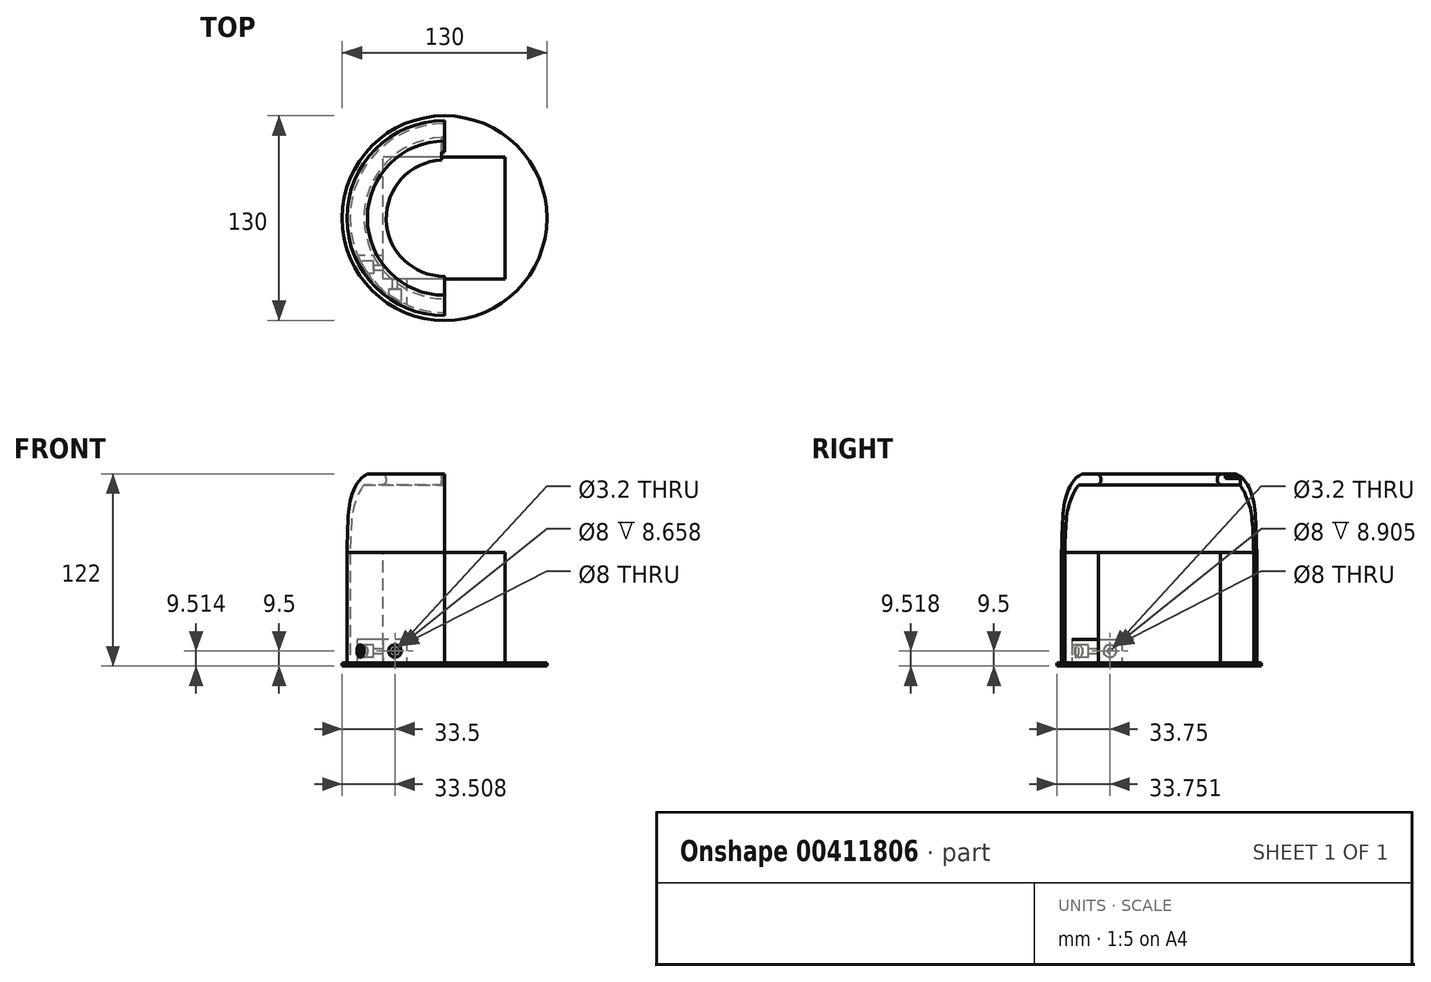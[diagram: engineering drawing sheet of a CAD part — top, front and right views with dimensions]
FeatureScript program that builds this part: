
annotation { "Feature Type Name" : "Feature", "Feature Type Description" : "" }
export const myFeature = defineFeature(function(context is Context, id is Id, definition is map)
    precondition{}
    {
        {
            var Q0;
            Q0=qCreatedBy(makeId("Front.planeOp"),FACE);
            var sketch = newSketch(context, id + "F0", { "sketchPlane" : qUnion([Q0])});
            skLineSegment(sketch, "E0", {"start": v(-40, 50) * mm, "end": v(-49, 50) * mm});
            skLineSegment(sketch, "E1", {"start": v(-62, 0) * mm, "end": v(-62, -70) * mm});
            skLineSegment(sketch, "E2", {"start": v(-37, 47) * mm, "end": v(-37, 46) * mm});
            skLineSegment(sketch, "E3", {"start": v(-40, 43) * mm, "end": v(-51.2, 43) * mm});
            skFitSpline(sketch, "E4", {"points": [v(-49, 50) * mm, v(-52.64, 47.47) * mm, v(-56.76, 41.98) * mm, v(-60.39, 29.9) * mm, v(-62, 0) * mm], "startDerivative": vector(-21.37, -10.6) * mm, "endDerivative": vector(-3.86, -109.3) * mm});
            skPoint(sketch, "E5.visualSharp", {"position": v(-37, 50) * mm});
            skArc(sketch, "E5.filletArc", {"start": v(-37, 47) * mm, "mid": v(-37.88, 49.12) * mm, "end": v(-40, 50) * mm});
            skPoint(sketch, "E6.visualSharp", {"position": v(-37, 43) * mm});
            skArc(sketch, "E6.filletArc", {"start": v(-40, 43) * mm, "mid": v(-37.88, 43.88) * mm, "end": v(-37, 46) * mm});
            skFitSpline(sketch, "E7", {"points": [v(-51.2, 43) * mm, v(-53.22, 40.09) * mm, v(-57.32, 30.2) * mm, v(-60, 0) * mm], "startDerivative": vector(-23.74, -33.12) * mm, "endDerivative": vector(-3.58, -89.87) * mm});
            skLineSegment(sketch, "E8", {"start": v(-62, -70) * mm, "end": v(0, -70) * mm});
            skLineSegment(sketch, "E9", {"start": v(0, -70) * mm, "end": v(0, -69.08) * mm});
            skLineSegment(sketch, "E10", {"start": v(-60, 0) * mm, "end": v(-60, -70) * mm});
            skSolve(sketch);
        }
        {
            var Q0;
            Q0=makeQuery(id+"F0.imprint","IMPRINT",FACE,{"disambiguationData":[TD([[makeQuery(id+"F0.imprint","IMPRINT",EDGE,{"derivedFrom":sQuery(id+"F0.wireOp",EDGE,"E0")}),1.0]])]});
            var Q1;
            Q1=sQuery(id+"F0.wireOp",EDGE,"E9");
            revolve(context, id + "F1", {"entities" : qUnion([Q0]), "axis" : qUnion([Q1]), "revolveType" : RevolveType.SYMMETRIC, "angle" : 180 * degree});
        }
        {
            var Q0;
            Q0=qCreatedBy(makeId("Front.planeOp"),FACE);
            var sketch = newSketch(context, id + "F2", { "sketchPlane" : qUnion([Q0])});
            skCircle(sketch, "E11", {"center": v(0, 47) * mm, "radius": 2 * mm});
            skLineSegment(sketch, "E12", {"start": v(-2, 47.07) * mm, "end": v(-2, 42.07) * mm});
            skLineSegment(sketch, "E13", {"start": v(-2, 42.07) * mm, "end": v(0, 42.07) * mm});
            skLineSegment(sketch, "E14", {"start": v(0, 42.07) * mm, "end": v(0, 45) * mm});
            skLineSegment(sketch, "E15", {"start": v(-2, 47.07) * mm, "end": v(-2, 50.36) * mm});
            skLineSegment(sketch, "E16", {"start": v(0, 50.36) * mm, "end": v(0, 49) * mm});
            skLineSegment(sketch, "E17", {"start": v(-2, 50.36) * mm, "end": v(0, 50.36) * mm});
            skSolve(sketch);
        }
        {
            var Q0;
            {var subQ1=sQuery(id+"F2.wireOp",EDGE,"E11");var subQ4=makeQuery(id+"F2.imprint","INTERSECT",VERTEX,{"derivedFrom":[subQ1,sQuery(id+"F2.wireOp",EDGE,"E14")]});Q0=makeQuery(id+"F2.imprint","IMPRINT",FACE,{"disambiguationData":[TD([[makeQuery(id+"F2.imprint","IMPRINT",EDGE,{"disambiguationData":[TD([[subQ4,1.0]])],"derivedFrom":subQ1}),1.0]])]});}
            extrude(context, id + "F3", {"entities" : qUnion([Q0]), "operationType" : NewBodyOperationType.REMOVE, "oppositeDirection" : true, "depth" : 49 * mm});
        }
        {
            var Q0;
            {var subQ0=sQuery(id+"F2.wireOp",EDGE,"E15");Q0=makeQuery(id+"F2.imprint","IMPRINT",FACE,{"disambiguationData":[TD([[makeQuery(id+"F2.imprint","IMPRINT",EDGE,{"derivedFrom":subQ0}),-1.0]])]});}
            extrude(context, id + "F4", {"entities" : qUnion([Q0]), "operationType" : NewBodyOperationType.REMOVE, "oppositeDirection" : true, "depth" : 42 * mm});
        }
        {
            var Q0;
            {var subQ4=sQuery(id+"F2.wireOp",EDGE,"E13");Q0=makeQuery(id+"F2.imprint","IMPRINT",FACE,{"disambiguationData":[TD([[makeQuery(id+"F2.imprint","IMPRINT",EDGE,{"derivedFrom":subQ4}),1.0]])]});}
            extrude(context, id + "F5", {"entities" : qUnion([Q0]), "operationType" : NewBodyOperationType.REMOVE, "oppositeDirection" : true, "depth" : 51.5 * mm});
        }
        {
            var Q0;
            Q0=qCreatedBy(makeId("Right.planeOp"),FACE);
            var sketch = newSketch(context, id + "F6", { "sketchPlane" : qUnion([Q0])});
            skLineSegment(sketch, "E18.bottom", {"start": v(49, 47) * mm, "end": v(51.5, 47) * mm});
            skLineSegment(sketch, "E18.top", {"start": v(49, 44) * mm, "end": v(51.5, 44) * mm});
            skLineSegment(sketch, "E18.left", {"start": v(49, 47) * mm, "end": v(49, 44) * mm});
            skLineSegment(sketch, "E18.right", {"start": v(51.5, 47) * mm, "end": v(51.5, 44) * mm});
            skSolve(sketch);
        }
        {
            var Q0;
            Q0=makeQuery(id+"F6.imprint","IMPRINT",FACE,{"disambiguationData":[TD([[makeQuery(id+"F6.imprint","IMPRINT",EDGE,{"derivedFrom":sQuery(id+"F6.wireOp",EDGE,"E18.bottom")}),-1.0]])]});
            extrude(context, id + "F7", {"entities" : qUnion([Q0]), "operationType" : NewBodyOperationType.REMOVE, "oppositeDirection" : true, "depth" : 2 * mm});
        }
        {
            var Q0;
            Q0=qCreatedBy(makeId("Top.planeOp"),FACE);
            var sketch = newSketch(context, id + "F8", { "sketchPlane" : qUnion([Q0])});
            skLineSegment(sketch, "E19.bottom", {"start": v(38.5, -38.75) * mm, "end": v(-39, -38.75) * mm});
            skLineSegment(sketch, "E19.top", {"start": v(38.5, 38.75) * mm, "end": v(-39, 38.75) * mm});
            skLineSegment(sketch, "E19.left", {"start": v(38.5, -38.75) * mm, "end": v(38.5, 38.75) * mm});
            skLineSegment(sketch, "E19.right", {"start": v(-39, -38.75) * mm, "end": v(-39, 38.75) * mm});
            skSolve(sketch);
        }
        {
            var Q0;
            Q0=makeQuery(id+"F8.imprint","IMPRINT",FACE,{"disambiguationData":[TD([[makeQuery(id+"F8.imprint","IMPRINT",EDGE,{"derivedFrom":sQuery(id+"F8.wireOp",EDGE,"E19.bottom")}),-1.0]])]});
            extrude(context, id + "F9", {"entities" : qUnion([Q0]), "operationType" : NewBodyOperationType.ADD, "oppositeDirection" : true, "depth" : 70 * mm});
        }
        {
            var Q0;
            Q0=makeQuery(id+"F9.opExtrude","CAP_FACE",FACE,{"disambiguationData":[OSD([sQuery(id+"F8.wireOp",EDGE,"E19.bottom"),sQuery(id+"F8.wireOp",EDGE,"E19.top"),sQuery(id+"F8.wireOp",EDGE,"E19.left"),sQuery(id+"F8.wireOp",EDGE,"E19.right")])],"isStart":false});
            var sketch = newSketch(context, id + "F10", { "sketchPlane" : qUnion([Q0])});
            skLineSegment(sketch, "E20", {"start": v(-39, 38.75) * mm, "end": v(-39, 23.75) * mm});
            skLineSegment(sketch, "E21", {"start": v(-39, 23.75) * mm, "end": v(-55.5, 23.75) * mm});
            skLineSegment(sketch, "E22", {"start": v(-39, 38.75) * mm, "end": v(-24, 38.75) * mm});
            skLineSegment(sketch, "E23", {"start": v(-24, 38.75) * mm, "end": v(-24, 55.25) * mm});
            skArc(sketch, "E24", {"start": v(-24, 55.25) * mm, "mid": v(-42.86, 42.6) * mm, "end": v(-55.5, 23.75) * mm});
            skSolve(sketch);
        }
        {
            var Q0;
            Q0=makeQuery(id+"F10.imprint","IMPRINT",FACE,{"disambiguationData":[TD([[makeQuery(id+"F10.imprint","IMPRINT",EDGE,{"derivedFrom":sQuery(id+"F10.wireOp",EDGE,"E20")}),-1.0]])]});
            extrude(context, id + "F11", {"entities" : qUnion([Q0]), "oppositeDirection" : true, "depth" : 15 * mm});
        }
        {
            var Q0;
            Q0=makeQuery(id+"F11.opExtrude","SWEPT_FACE",FACE,{"disambiguationData":[OSD([sQuery(id+"F10.wireOp",EDGE,"E20")])]});
            var sketch = newSketch(context, id + "F12", { "sketchPlane" : qUnion([Q0])});
            skCircle(sketch, "E25", {"center": v(-31.25, -62.5) * mm, "radius": 1.6 * mm});
            skSolve(sketch);
        }
        {
            var Q0;
            Q0=makeQuery(id+"F12.imprint","IMPRINT",FACE,{"disambiguationData":[TD([[makeQuery(id+"F12.imprint","IMPRINT",EDGE,{"derivedFrom":sQuery(id+"F12.wireOp",EDGE,"E25")}),1.0]])]});
            extrude(context, id + "F13", {"entities" : qUnion([Q0]), "operationType" : NewBodyOperationType.REMOVE, "oppositeDirection" : true, "depth" : 15 * mm});
        }
        {
            var Q0;
            Q0=qCreatedBy(makeId("Right.planeOp"),FACE);
            cPlane(context, id + "F14", {"entities" : qUnion([Q0]), "cplaneType" : CPlaneType.OFFSET, "offset" : 60 * mm, "oppositeDirection" : true, "width" : 150 * mm, "height" : 150 * mm});
        }
        {
            var Q0;
            Q0=qCreatedBy(id+"F14.planeOp",FACE);
            var sketch = newSketch(context, id + "F15", { "sketchPlane" : qUnion([Q0])});
            skCircle(sketch, "E26", {"center": v(-31.25, -62.48) * mm, "radius": 4 * mm});
            skSolve(sketch);
        }
        {
            var Q0;
            Q0 = qSketchRegion(id + "F15", true);
            extrude(context, id + "F16", {"entities" : qUnion([Q0]), "operationType" : NewBodyOperationType.REMOVE, "depth" : 15 * mm});
        }
        {
            var Q0;
            Q0=makeQuery(id+"F11.opExtrude","SWEPT_FACE",FACE,{"disambiguationData":[OSD([sQuery(id+"F10.wireOp",EDGE,"E22")])]});
            var sketch = newSketch(context, id + "F17", { "sketchPlane" : qUnion([Q0])});
            skCircle(sketch, "E27", {"center": v(31.5, -62.5) * mm, "radius": 1.6 * mm});
            skSolve(sketch);
        }
        {
            var Q0;
            Q0=makeQuery(id+"F17.imprint","IMPRINT",FACE,{"disambiguationData":[TD([[makeQuery(id+"F17.imprint","IMPRINT",EDGE,{"derivedFrom":sQuery(id+"F17.wireOp",EDGE,"E27")}),1.0]])]});
            extrude(context, id + "F18", {"entities" : qUnion([Q0]), "operationType" : NewBodyOperationType.REMOVE, "oppositeDirection" : true, "depth" : 15 * mm});
        }
        {
            var Q0;
            Q0=qCreatedBy(makeId("Front.planeOp"),FACE);
            cPlane(context, id + "F19", {"entities" : qUnion([Q0]), "cplaneType" : CPlaneType.OFFSET, "offset" : 60 * mm, "width" : 150 * mm, "height" : 150 * mm});
        }
        {
            var Q0;
            Q0=qCreatedBy(id+"F19.planeOp",FACE);
            var sketch = newSketch(context, id + "F20", { "sketchPlane" : qUnion([Q0])});
            skCircle(sketch, "E28", {"center": v(-31.5, -62.49) * mm, "radius": 4 * mm});
            skSolve(sketch);
        }
        {
            var Q0;
            Q0 = qSketchRegion(id + "F20", true);
            extrude(context, id + "F21", {"entities" : qUnion([Q0]), "operationType" : NewBodyOperationType.REMOVE, "oppositeDirection" : true, "depth" : 15 * mm});
        }
        {
            var Q0;
            Q0=qCreatedBy(makeId("Front.planeOp"),FACE);
            var sketch = newSketch(context, id + "F22", { "sketchPlane" : qUnion([Q0])});
            skLineSegment(sketch, "E29.bottom", {"start": v(0, -70) * mm, "end": v(-65, -70) * mm});
            skLineSegment(sketch, "E29.top", {"start": v(0, -72) * mm, "end": v(-65, -72) * mm});
            skLineSegment(sketch, "E29.left", {"start": v(0, -70) * mm, "end": v(0, -72) * mm});
            skLineSegment(sketch, "E29.right", {"start": v(-65, -70) * mm, "end": v(-65, -72) * mm});
            skLineSegment(sketch, "E30.bottom", {"start": v(-65, -70) * mm, "end": v(-62.2, -70) * mm});
            skLineSegment(sketch, "E30.top", {"start": v(-65, -67.15) * mm, "end": v(-62.2, -67.15) * mm});
            skLineSegment(sketch, "E30.left", {"start": v(-65, -70) * mm, "end": v(-65, -67.15) * mm});
            skLineSegment(sketch, "E30.right", {"start": v(-62.2, -70) * mm, "end": v(-62.2, -67.15) * mm});
            skLineSegment(sketch, "E31.bottom", {"start": v(-59.9, -70) * mm, "end": v(-55.4, -70) * mm});
            skLineSegment(sketch, "E31.top", {"start": v(-59.9, -60) * mm, "end": v(-55.4, -60) * mm});
            skLineSegment(sketch, "E31.left", {"start": v(-59.9, -70) * mm, "end": v(-59.9, -60) * mm});
            skLineSegment(sketch, "E31.right", {"start": v(-55.4, -70) * mm, "end": v(-55.4, -60) * mm});
            skSolve(sketch);
        }
        {
            var Q0;
            Q0=makeQuery(id+"F22.imprint","IMPRINT",FACE,{"disambiguationData":[TD([[makeQuery(id+"F22.imprint","IMPRINT",EDGE,{"derivedFrom":sQuery(id+"F22.wireOp",EDGE,"E30.bottom")}),1.0]])]});
            var Q1;
            Q1=makeQuery(id+"F22.imprint","IMPRINT",FACE,{"disambiguationData":[TD([[makeQuery(id+"F22.imprint","IMPRINT",EDGE,{"derivedFrom":sQuery(id+"F22.wireOp",EDGE,"E29.top")}),-1.0]])]});
            var Q2;
            Q2=makeQuery(id+"F22.imprint","IMPRINT",FACE,{"disambiguationData":[TD([[makeQuery(id+"F22.imprint","IMPRINT",EDGE,{"derivedFrom":sQuery(id+"F22.wireOp",EDGE,"E31.bottom")}),1.0]])]});
            var Q3;
            Q3=sQuery(id+"F0.wireOp",EDGE,"E9");
            revolve(context, id + "F23", {"entities" : qUnion([Q0, Q1, Q2]), "axis" : qUnion([Q3]), "revolveType" : RevolveType.FULL});
        }
    });
